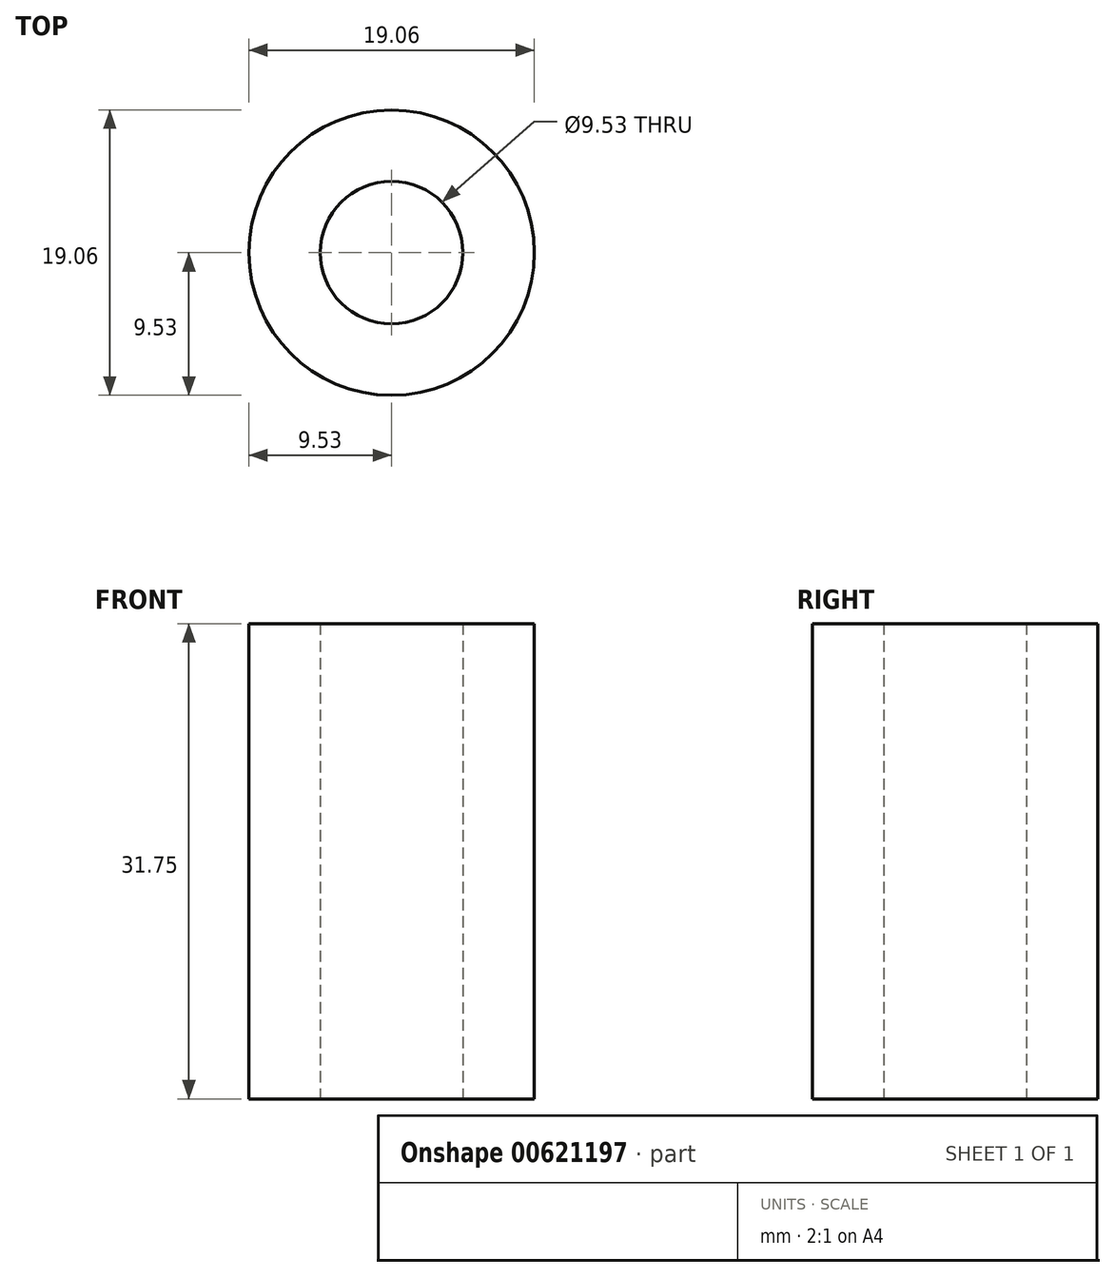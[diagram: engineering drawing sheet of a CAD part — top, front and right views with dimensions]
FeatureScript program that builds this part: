
annotation { "Feature Type Name" : "Feature", "Feature Type Description" : "" }
export const myFeature = defineFeature(function(context is Context, id is Id, definition is map)
    precondition{}
    {
        {
            var Q0;
            Q0=qCreatedBy(makeId("Top.planeOp"),FACE);
            var sketch = newSketch(context, id + "F0", { "sketchPlane" : qUnion([Q0])});
            skCircle(sketch, "E0", {"center": v(0, 0) * mm, "radius": 4.76 * mm});
            skCircle(sketch, "E1", {"center": v(0, 0) * mm, "radius": 9.53 * mm});
            skSolve(sketch);
        }
        {
            var Q0;
            Q0=makeQuery(id+"F0.imprint","IMPRINT",FACE,{"disambiguationData":[TD([[makeQuery(id+"F0.imprint","IMPRINT",EDGE,{"derivedFrom":sQuery(id+"F0.wireOp",EDGE,"E0")}),-1.0]])]});
            extrude(context, id + "F1", {"entities" : qUnion([Q0]), "depth" : 31.75 * mm, "offsetDistance" : 25.4 * mm});
        }
    });
